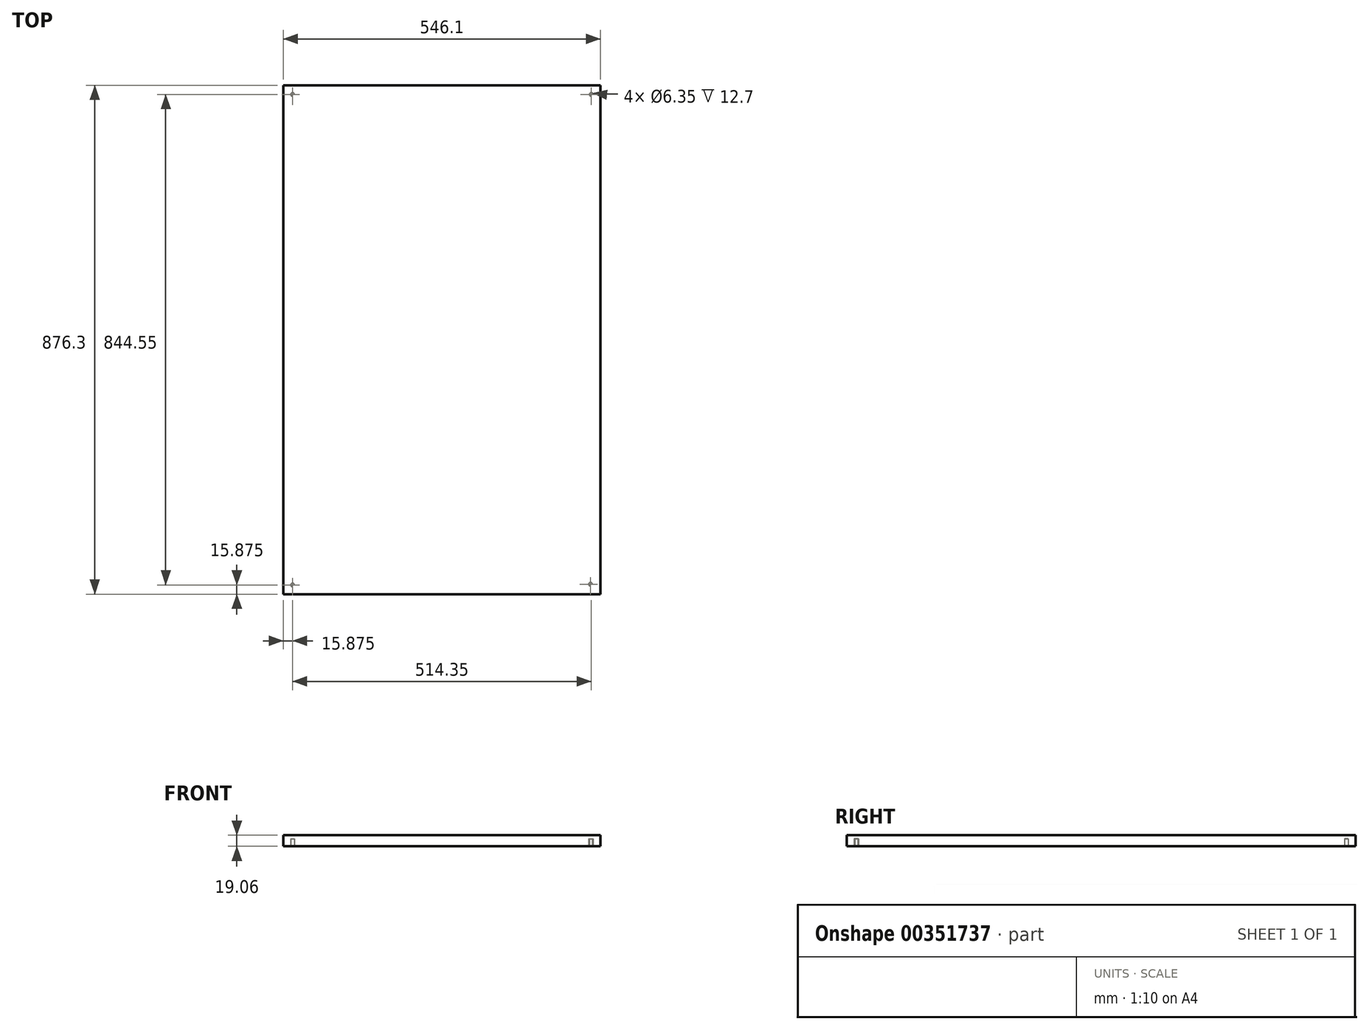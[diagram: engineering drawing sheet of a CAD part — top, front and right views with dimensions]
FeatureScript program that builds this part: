
annotation { "Feature Type Name" : "Feature", "Feature Type Description" : "" }
export const myFeature = defineFeature(function(context is Context, id is Id, definition is map)
    precondition{}
    {
        {
            var Q0;
            Q0=qCreatedBy(makeId("Front.planeOp"),FACE);
            var sketch = newSketch(context, id + "F0", { "sketchPlane" : qUnion([Q0])});
            skLineSegment(sketch, "E0.bottom", {"start": v(-273.05, 9.52) * mm, "end": v(273.05, 9.53) * mm});
            skLineSegment(sketch, "E0.top", {"start": v(-273.05, -9.53) * mm, "end": v(273.05, -9.53) * mm});
            skLineSegment(sketch, "E0.left", {"start": v(-273.05, 9.52) * mm, "end": v(-273.05, -9.53) * mm});
            skLineSegment(sketch, "E0.right", {"start": v(273.05, 9.53) * mm, "end": v(273.05, -9.52) * mm});
            skPoint(sketch, "E0.middle", {"position": v(0, 0) * mm});
            skSolve(sketch);
        }
        {
            var Q0;
            Q0 = qSketchRegion(id + "F0", true);
            extrude(context, id + "F1", {"entities" : qUnion([Q0]), "endBound" : BoundingType.SYMMETRIC, "depth" : 876.3 * mm});
        }
        {
            var Q0;
            Q0=makeQuery(id+"F1.opExtrude","SWEPT_FACE",FACE,{"disambiguationData":[OSD([sQuery(id+"F0.wireOp",EDGE,"E0.top")])]});
            var sketch = newSketch(context, id + "F2", { "sketchPlane" : qUnion([Q0])});
            skCircle(sketch, "E1", {"center": v(255.9, 421) * mm, "radius": 3.18 * mm});
            skCircle(sketch, "E2", {"center": v(257.18, -422.28) * mm, "radius": 3.18 * mm});
            skCircle(sketch, "E3", {"center": v(-257.18, -422.28) * mm, "radius": 3.18 * mm});
            skCircle(sketch, "E4", {"center": v(-257.18, 422.28) * mm, "radius": 3.18 * mm});
            skSolve(sketch);
        }
        {
            var Q0;
            Q0=makeQuery(id+"F2.imprint","IMPRINT",FACE,{"disambiguationData":[TD([[makeQuery(id+"F2.imprint","IMPRINT",EDGE,{"derivedFrom":sQuery(id+"F2.wireOp",EDGE,"E1")}),1.0]])]});
            var Q1;
            Q1=makeQuery(id+"F2.imprint","IMPRINT",FACE,{"disambiguationData":[TD([[makeQuery(id+"F2.imprint","IMPRINT",EDGE,{"derivedFrom":sQuery(id+"F2.wireOp",EDGE,"E2")}),1.0]])]});
            var Q2;
            Q2=makeQuery(id+"F2.imprint","IMPRINT",FACE,{"disambiguationData":[TD([[makeQuery(id+"F2.imprint","IMPRINT",EDGE,{"derivedFrom":sQuery(id+"F2.wireOp",EDGE,"E3")}),1.0]])]});
            var Q3;
            Q3=makeQuery(id+"F2.imprint","IMPRINT",FACE,{"disambiguationData":[TD([[makeQuery(id+"F2.imprint","IMPRINT",EDGE,{"derivedFrom":sQuery(id+"F2.wireOp",EDGE,"E4")}),1.0]])]});
            extrude(context, id + "F3", {"entities" : qUnion([Q0, Q1, Q2, Q3]), "operationType" : NewBodyOperationType.REMOVE, "oppositeDirection" : true, "depth" : 12.7 * mm, "offsetDistance" : 25.4 * mm});
        }
    });
